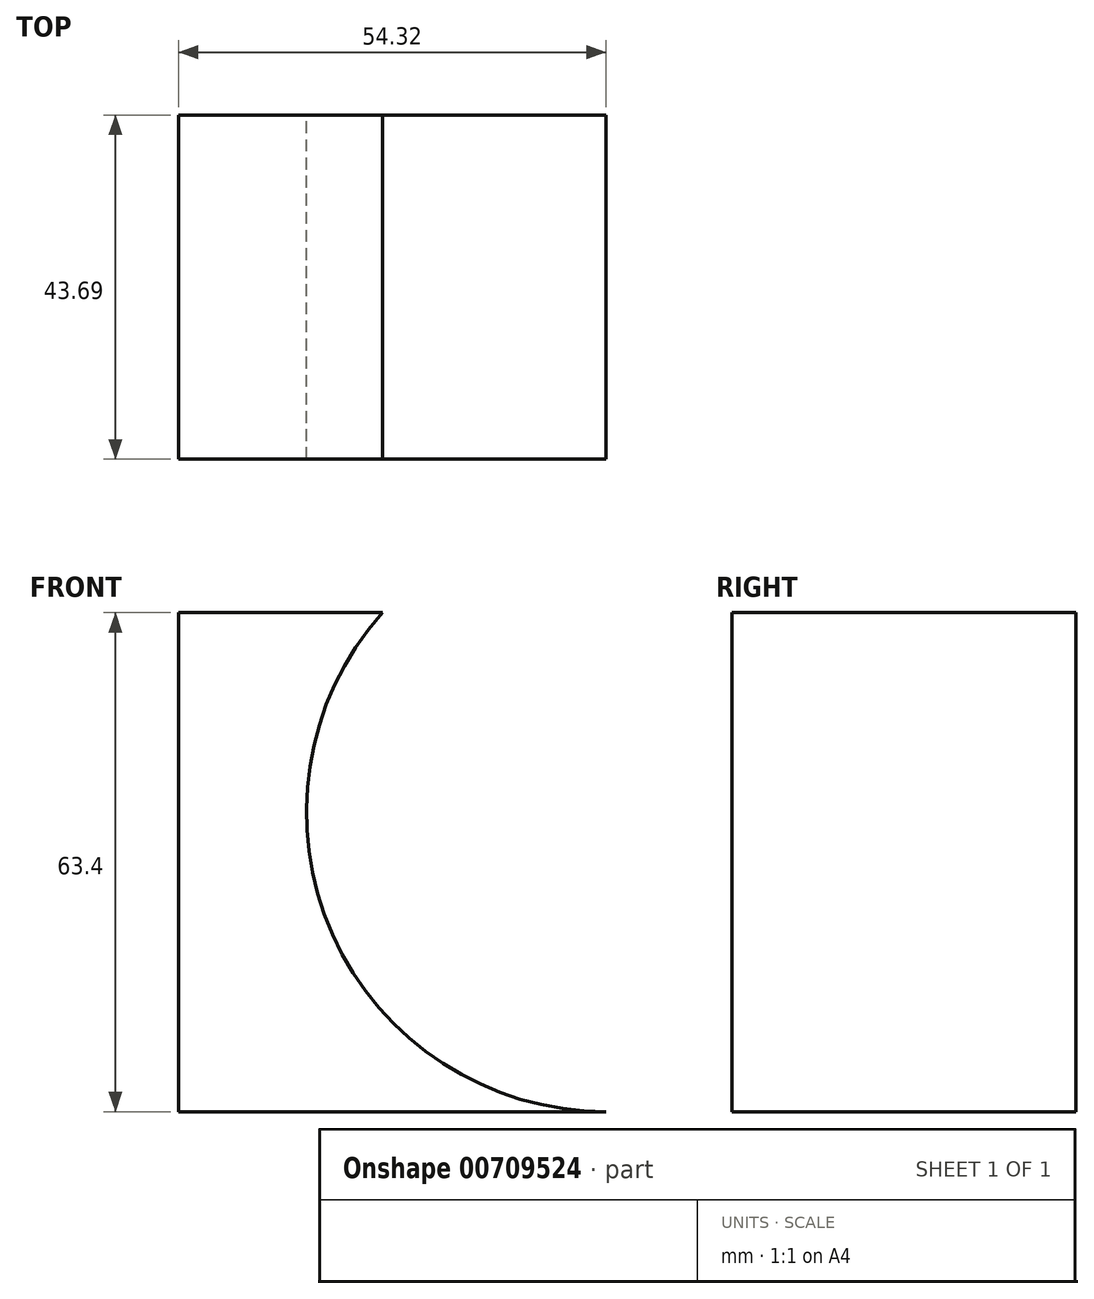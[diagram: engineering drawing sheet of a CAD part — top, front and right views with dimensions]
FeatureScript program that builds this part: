
annotation { "Feature Type Name" : "Feature", "Feature Type Description" : "" }
export const myFeature = defineFeature(function(context is Context, id is Id, definition is map)
    precondition{}
    {
        {
            var Q0;
            Q0=qCreatedBy(makeId("Front.planeOp"),FACE);
            var sketch = newSketch(context, id + "F0", { "sketchPlane" : qUnion([Q0])});
            skLineSegment(sketch, "E0", {"start": v(-54.32, 63.4) * mm, "end": v(-54.32, 0) * mm});
            skLineSegment(sketch, "E1", {"start": v(-54.32, 0) * mm, "end": v(0, 0) * mm});
            skLineSegment(sketch, "E2", {"start": v(-54.32, 63.4) * mm, "end": v(-28.4, 63.4) * mm});
            skArc(sketch, "E3", {"start": v(-28.4, 63.4) * mm, "mid": v(-34.73, 22.5) * mm, "end": v(0, 0) * mm});
            skSolve(sketch);
        }
        {
            var Q0;
            Q0 = qSketchRegion(id + "F0", true);
            extrude(context, id + "F1", {"entities" : qUnion([Q0]), "depth" : 43.69 * mm, "offsetDistance" : 25.4 * mm});
        }
    });
